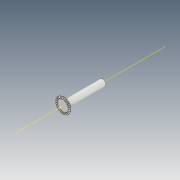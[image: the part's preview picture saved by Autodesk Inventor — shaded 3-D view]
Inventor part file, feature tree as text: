
AUTODESK INVENTOR PART (.ipt)
format: ipt  version: 2021 (Build 250183000, 183)  size: 499,200 bytes
history: native  units: mm
features: other x16, sketch x10, loft x3, pattern_circular x3, extrude x1
ambient origin geometry x6: Origin, XZ Plane, X Axis, Y Axis, Z Axis, Center Point
bodies: Solid1 (feature_tree)
feature tree (33):
  other  "Ponto superior"
  other  "Plano de malha 2"
  other  "Corpo dentado"
  other  "Ponto inicial"
  other  "Plano de dente"
  sketch  "Esboço inicial"  dims[d3=0.6mm]
  other  "Extremidade"
  loft  "Loft"
  pattern_circular  "Circular Pattern"  [2 undecoded]
  sketch  "Esboço 3D direito"  dims[d4=1.194087mm]
  other  "Plano final direito"
  loft  "Transição direita"
  pattern_circular  "Padrão circular direito"  Angle=90.0deg  [1 undecoded]
  sketch  "Esboço 3D esquerdo"  dims[d5=90.0deg]
  other  "Plano final esquerdo"
  loft  "Transição esquerda"
  pattern_circular  "Padrão circular esquerdo"  Angle=360.0deg  [1 undecoded]
  other  "Fixar corpo"
  extrude  "Extrusão1"  Depth=10.0mm
  other  "Plano de malha"
  other  "Plano superior"
  sketch  "Esboço de corpo dentado"  dims[d7=1.663639mm]
  other  "Plano final"
  sketch  "Esboço final"  dims[d8=1.691227mm]
  other  "Helical Curve Left"
  sketch  "Esboço final esquerdo"  dims[d9=4.071779mm]
  sketch  "Esboço de corpo"  dims[d11=0.6198mm]
  sketch  "Sketch6"  dims[d0=4.68mm d1=4.46412mm]
  other  "Srf1"
  other  "Helical Curve Right"
  sketch  "Esboço final direita"  dims[d12=1.281954mm d15=1.303212mm d16=3.137599mm d17=0.0mm d18=90.0deg d19=0.0mm d20=90.0deg d21=260.0mm d22=360.0deg d26=17.944705mm d27=0.309728mm d28=4.68mm d29=-10.47518mm d30=1.281954mm d31=1.303212mm d32=3.137599mm d35=0.0mm d37=0.0mm d39=0.0mm d40=90.0deg d41=260.0mm d42=360.0deg d46=90.0deg d47=90.0deg d48=0.0mm d49=0.0mm d50=90.0deg d51=1.208305mm d52=0.0mm d53=0.0mm d54=0.0mm d56=0.94732mm d57=4.981399mm d58=4.419079mm d59=3.838526mm d60=3.405218mm d61=3.838526mm d62=3.405218mm d65=17.944705mm d66=31.5mm d67=4.68mm d68=-10.47518mm d69=0.309728mm d70=1.303212mm d71=3.137599mm d72=1.281954mm d73=3.405218mm d74=3.838526mm d75=0.0mm d77=0.0mm d79=0.0mm d80=90.0deg d81=260.0mm d82=360.0deg d84=10.0mm d85=20.0mm d86=20.0mm d87=10.0mm d88=0.0mm d89=0.0mm d90=90.0deg d91=90.0deg d92=90.0deg d93=90.0deg d94=12.5mm d95=0.0mm]
  sketch  "Esboço8"  dims[d2=4.8599mm]
  other  "Diâmetro do flanco"
note: 4 required parameter values undecoded (feature->parameter linkage not recoverable at this tier; creation-order binding heuristic only, values carry confidence <= 0.55)
